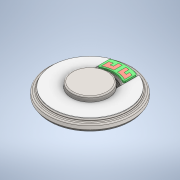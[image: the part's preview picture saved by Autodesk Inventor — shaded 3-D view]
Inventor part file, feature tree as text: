
AUTODESK INVENTOR PART (.ipt)
format: ipt  version: 2020 (Build 240168000, 168)  size: 1,307,648 bytes
history: native  units: mm
features: other x6, helix x1
ambient origin geometry x8: Origin, YZ Plane, XZ Plane, XY Plane, X Axis, Y Axis, Z Axis, Center Point
bodies: Solid1 (feature_tree), Solid2 (feature_tree), Solid3 (feature_tree), Solid4 (feature_tree), Solid5 (feature_tree), Solid6 (feature_tree), Solid7 (feature_tree)
feature tree (7):
  other  "Fabric cover extrude"
  other  "Magnet fillets"
  other  "Micro cutout"
  other  "Diaphragm revolve"
  other  "Isolation ring"
  helix  "Coil position"  [1 undecoded]
  other  "Soldering pads"
note: 1 required parameter value undecoded (feature->parameter linkage not recoverable at this tier; creation-order binding heuristic only, values carry confidence <= 0.55)
